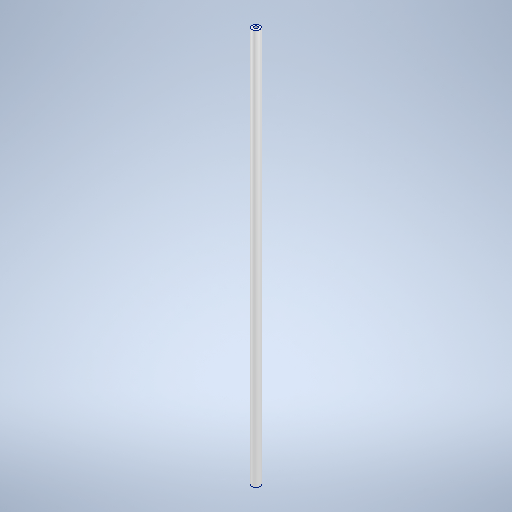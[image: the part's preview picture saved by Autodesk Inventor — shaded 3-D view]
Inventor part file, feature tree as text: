
AUTODESK INVENTOR PART (.ipt)
format: ipt  version: 2025 (Build 290162000, 162)  size: 261,120 bytes
history: native  units: mm
features: sketch x2, other x1, extrude x1, hole x1, mirror x1
ambient origin geometry x8: Origin, YZ Plane, XZ Plane, XY Plane, X Axis, Y Axis, Z Axis, Center Point
bodies: Body1 (feature_tree)
feature tree (6):
  other  "Těleso1"
  extrude  "Vysunutí1"  Depth=5.0mm
  hole  "Díra1"  [1 undecoded]
  mirror  "Zrcadlit1"
  sketch  "Náčrt1"
  sketch  "Náčrt2"
note: 1 required parameter value undecoded (feature->parameter linkage not recoverable at this tier; creation-order binding heuristic only, values carry confidence <= 0.55)
